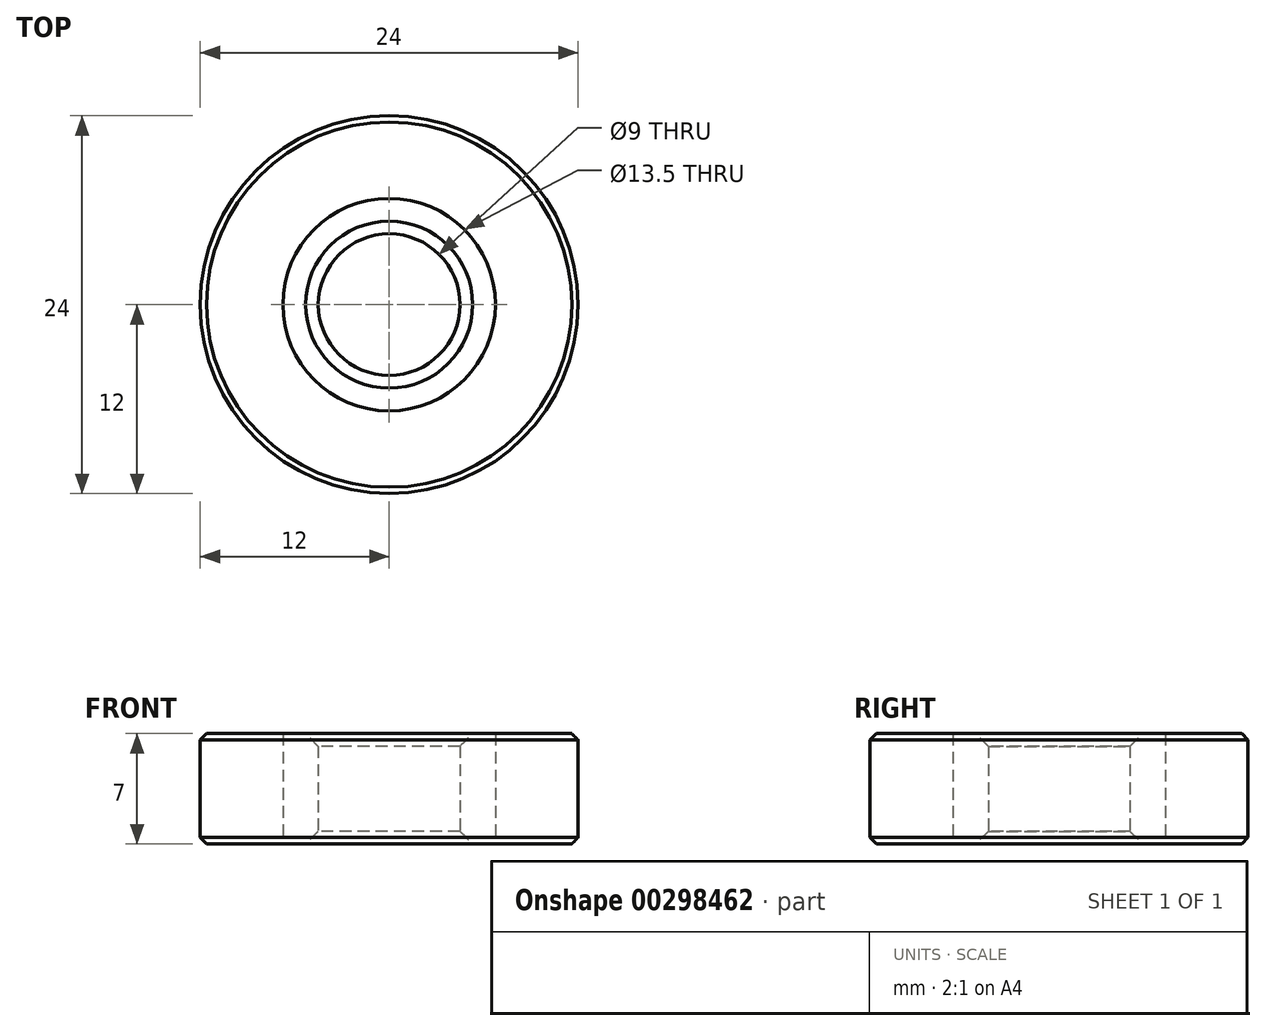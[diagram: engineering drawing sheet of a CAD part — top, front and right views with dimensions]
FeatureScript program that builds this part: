
annotation { "Feature Type Name" : "Feature", "Feature Type Description" : "" }
export const myFeature = defineFeature(function(context is Context, id is Id, definition is map)
    precondition{}
    {
        {
            var Q0;
            Q0=qCreatedBy(makeId("Top.planeOp"),FACE);
            var sketch = newSketch(context, id + "F0", { "sketchPlane" : qUnion([Q0])});
            skCircle(sketch, "E0", {"center": v(0, 0) * mm, "radius": 12 * mm});
            skCircle(sketch, "E1", {"center": v(0, 0) * mm, "radius": 4.5 * mm});
            skCircle(sketch, "E2", {"center": v(0, 0) * mm, "radius": 6.75 * mm});
            skSolve(sketch);
        }
        {
            var Q0;
            Q0=makeQuery(id+"F0.imprint","IMPRINT",FACE,{"disambiguationData":[TD([[makeQuery(id+"F0.imprint","IMPRINT",EDGE,{"derivedFrom":sQuery(id+"F0.wireOp",EDGE,"E0")}),1.0]])]});
            extrude(context, id + "F1", {"entities" : qUnion([Q0]), "depth" : 7 * mm});
        }
        {
            var Q0;
            Q0=makeQuery(id+"F0.imprint","IMPRINT",FACE,{"disambiguationData":[TD([[makeQuery(id+"F0.imprint","IMPRINT",EDGE,{"derivedFrom":sQuery(id+"F0.wireOp",EDGE,"E1")}),-1.0]])]});
            extrude(context, id + "F2", {"entities" : qUnion([Q0]), "depth" : 7 * mm});
        }
        {
            var Q0;
            Q0=makeQuery(id+"F1.opExtrude","CAP_EDGE",EDGE,{"disambiguationData":[OSD([sQuery(id+"F0.wireOp",EDGE,"E0")])],"isStart":false});
            var Q1;
            Q1=makeQuery(id+"F1.opExtrude","CAP_EDGE",EDGE,{"disambiguationData":[OSD([sQuery(id+"F0.wireOp",EDGE,"E0")])],"isStart":true});
            chamfer(context, id + "F3", {"entities" : qUnion([Q0, Q1]), "width" : 0.4 * mm, "tangentPropagation" : true});
        }
        {
            var Q0;
            Q0=makeQuery(id+"F2.opExtrude","CAP_EDGE",EDGE,{"disambiguationData":[OSD([sQuery(id+"F0.wireOp",EDGE,"E1")])],"isStart":false});
            var Q1;
            Q1=makeQuery(id+"F2.opExtrude","CAP_EDGE",EDGE,{"disambiguationData":[OSD([sQuery(id+"F0.wireOp",EDGE,"E1")])],"isStart":true});
            chamfer(context, id + "F4", {"entities" : qUnion([Q0, Q1]), "width" : 0.8 * mm, "tangentPropagation" : true});
        }
    });
